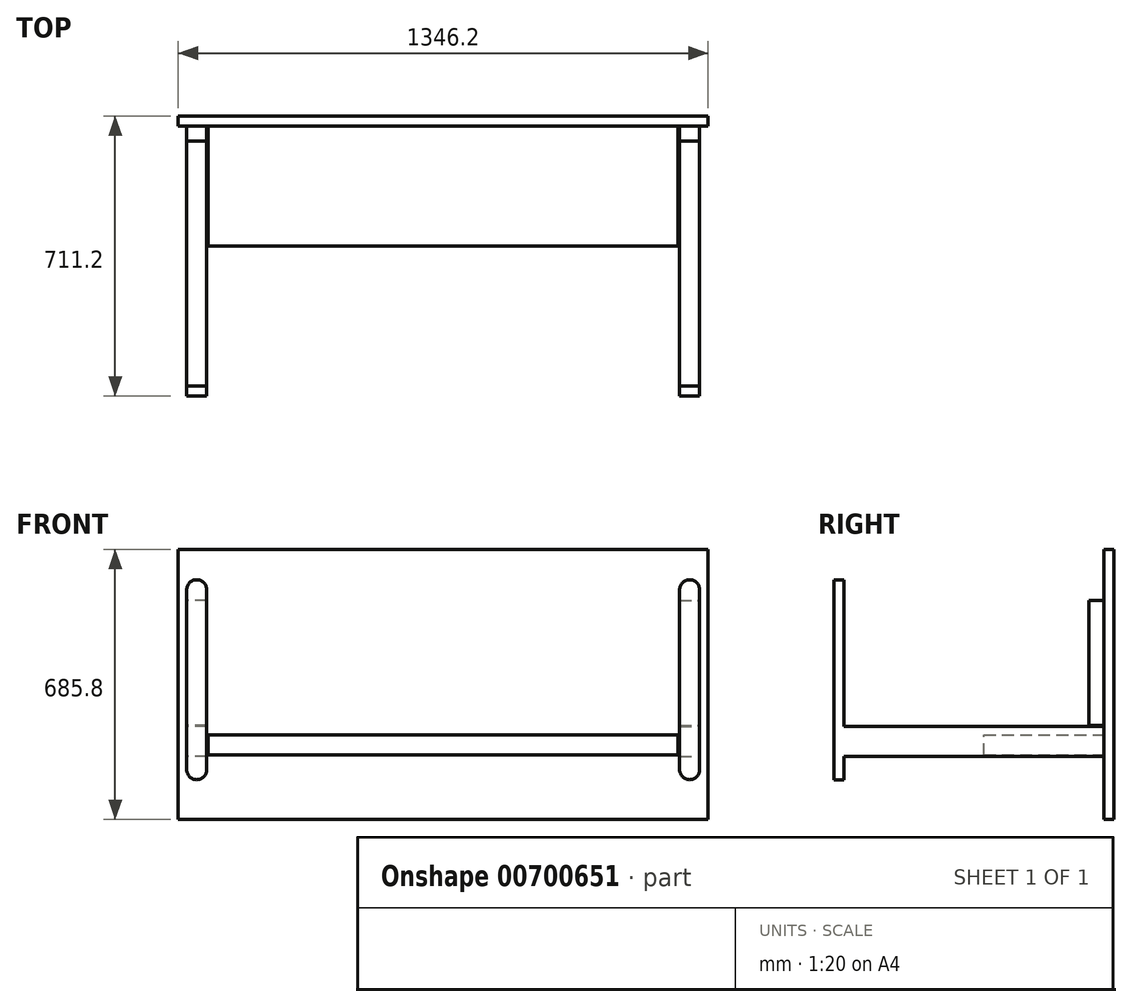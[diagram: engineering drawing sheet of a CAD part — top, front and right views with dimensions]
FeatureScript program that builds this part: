
annotation { "Feature Type Name" : "Feature", "Feature Type Description" : "" }
export const myFeature = defineFeature(function(context is Context, id is Id, definition is map)
    precondition{}
    {
        {
            var Q0;
            Q0=qCreatedBy(makeId("Front.planeOp"),FACE);
            var sketch = newSketch(context, id + "F0", { "sketchPlane" : qUnion([Q0])});
            skLineSegment(sketch, "E0.bottom", {"start": v(393.76, -264.72) * mm, "end": v(-952.44, -264.72) * mm});
            skLineSegment(sketch, "E0.top", {"start": v(393.76, 421.08) * mm, "end": v(-952.44, 421.08) * mm});
            skLineSegment(sketch, "E0.left", {"start": v(393.76, -264.72) * mm, "end": v(393.76, 421.08) * mm});
            skLineSegment(sketch, "E0.right", {"start": v(-952.44, -264.72) * mm, "end": v(-952.44, 421.08) * mm});
            skPoint(sketch, "E0.middle", {"position": v(-279.34, 78.18) * mm});
            skSolve(sketch);
        }
        {
            var Q0;
            Q0 = qSketchRegion(id + "F0", true);
            extrude(context, id + "F1", {"entities" : qUnion([Q0]), "depth" : 25.4 * mm, "offsetDistance" : 25.4 * mm});
        }
        {
            var Q0;
            Q0=makeQuery(id+"F1.opExtrude","CAP_FACE",FACE,{"disambiguationData":[OSD([sQuery(id+"F0.wireOp",EDGE,"E0.bottom"),sQuery(id+"F0.wireOp",EDGE,"E0.top"),sQuery(id+"F0.wireOp",EDGE,"E0.left"),sQuery(id+"F0.wireOp",EDGE,"E0.right")])],"isStart":false});
            var sketch = newSketch(context, id + "F2", { "sketchPlane" : qUnion([Q0])});
            skLineSegment(sketch, "E1", {"start": v(-279.34, 421.08) * mm, "end": v(-279.34, -264.72) * mm});
            skLineSegment(sketch, "E2.bottom", {"start": v(-879.77, -26.15) * mm, "end": v(-930.57, -26.15) * mm});
            skLineSegment(sketch, "E2.top", {"start": v(-879.77, 291.35) * mm, "end": v(-930.57, 291.35) * mm});
            skLineSegment(sketch, "E2.left", {"start": v(-879.77, -26.15) * mm, "end": v(-879.77, 291.35) * mm});
            skLineSegment(sketch, "E2.right", {"start": v(-930.57, -26.15) * mm, "end": v(-930.57, 291.35) * mm});
            skPoint(sketch, "E2.middle", {"position": v(-905.17, 132.6) * mm});
            skPoint(sketch, "E3.MirrorP", {"position": v(346.5, 132.6) * mm});
            skLineSegment(sketch, "E4.MirrorCS", {"start": v(321.1, -26.15) * mm, "end": v(321.1, 291.35) * mm});
            skLineSegment(sketch, "E5.MirrorCS", {"start": v(321.1, 291.35) * mm, "end": v(371.9, 291.35) * mm});
            skLineSegment(sketch, "E6.MirrorCS", {"start": v(371.9, -26.15) * mm, "end": v(371.9, 291.35) * mm});
            skLineSegment(sketch, "E7.MirrorCS", {"start": v(321.1, -26.15) * mm, "end": v(371.9, -26.15) * mm});
            skSolve(sketch);
        }
        {
            var Q0;
            Q0 = qSketchRegion(id + "F2", true);
            extrude(context, id + "F3", {"entities" : qUnion([Q0]), "operationType" : NewBodyOperationType.ADD, "depth" : 38.1 * mm, "offsetDistance" : 25.4 * mm});
        }
        {
            var Q0;
            Q0=makeQuery(id+"F1.opExtrude","CAP_FACE",FACE,{"disambiguationData":[OSD([sQuery(id+"F0.wireOp",EDGE,"E0.bottom"),sQuery(id+"F0.wireOp",EDGE,"E0.top"),sQuery(id+"F0.wireOp",EDGE,"E0.left"),sQuery(id+"F0.wireOp",EDGE,"E0.right")])],"isStart":false});
            var sketch = newSketch(context, id + "F4", { "sketchPlane" : qUnion([Q0])});
            skLineSegment(sketch, "E8.bottom", {"start": v(-880.2, -104.21) * mm, "end": v(-931, -104.21) * mm});
            skLineSegment(sketch, "E8.top", {"start": v(-880.2, -28.01) * mm, "end": v(-931, -28.01) * mm});
            skLineSegment(sketch, "E8.left", {"start": v(-880.2, -104.21) * mm, "end": v(-880.2, -28.01) * mm});
            skLineSegment(sketch, "E8.right", {"start": v(-931, -104.21) * mm, "end": v(-931, -28.01) * mm});
            skPoint(sketch, "E8.middle", {"position": v(-905.6, -66.11) * mm});
            skLineSegment(sketch, "E9", {"start": v(-279.34, 421.08) * mm, "end": v(-279.34, -264.72) * mm});
            skLineSegment(sketch, "E10.MirrorCS", {"start": v(372.32, -104.21) * mm, "end": v(372.32, -28.01) * mm});
            skLineSegment(sketch, "E11.MirrorCS", {"start": v(321.52, -104.21) * mm, "end": v(321.52, -28.01) * mm});
            skLineSegment(sketch, "E12.MirrorCS", {"start": v(321.52, -104.21) * mm, "end": v(372.32, -104.21) * mm});
            skLineSegment(sketch, "E13.MirrorCS", {"start": v(321.52, -28.01) * mm, "end": v(372.32, -28.01) * mm});
            skPoint(sketch, "E14.MirrorP", {"position": v(346.92, -66.11) * mm});
            skSolve(sketch);
        }
        {
            var Q0;
            Q0 = qSketchRegion(id + "F4", true);
            extrude(context, id + "F5", {"entities" : qUnion([Q0]), "operationType" : NewBodyOperationType.ADD, "depth" : 660.4 * mm, "offsetDistance" : 25.4 * mm});
        }
        {
            var Q0;
            Q0=makeQuery(id+"F5.opExtrude","CAP_FACE",FACE,{"disambiguationData":[OSD([sQuery(id+"F4.wireOp",EDGE,"E8.bottom"),sQuery(id+"F4.wireOp",EDGE,"E8.top"),sQuery(id+"F4.wireOp",EDGE,"E8.left"),sQuery(id+"F4.wireOp",EDGE,"E8.right")])],"isStart":false});
            var sketch = newSketch(context, id + "F6", { "sketchPlane" : qUnion([Q0])});
            skLineSegment(sketch, "E15.bottom", {"start": v(-905.6, 344.26) * mm, "end": v(-905.6, 344.26) * mm});
            skLineSegment(sketch, "E15.top", {"start": v(-905.6, -163.74) * mm, "end": v(-905.6, -163.74) * mm});
            skLineSegment(sketch, "E15.left", {"start": v(-880.2, 318.86) * mm, "end": v(-880.2, -138.34) * mm});
            skLineSegment(sketch, "E15.right", {"start": v(-931, 318.86) * mm, "end": v(-931, -138.34) * mm});
            skPoint(sketch, "E15.middle", {"position": v(-905.6, 90.26) * mm});
            skPoint(sketch, "E16.visualSharp", {"position": v(-880.2, 344.26) * mm});
            skArc(sketch, "E16.filletArc", {"start": v(-880.2, 318.86) * mm, "mid": v(-887.64, 336.82) * mm, "end": v(-905.6, 344.26) * mm});
            skPoint(sketch, "E17.visualSharp", {"position": v(-931, 344.26) * mm});
            skArc(sketch, "E17.filletArc", {"start": v(-905.6, 344.26) * mm, "mid": v(-923.56, 336.82) * mm, "end": v(-931, 318.86) * mm});
            skPoint(sketch, "E18.visualSharp", {"position": v(-880.2, -163.74) * mm});
            skArc(sketch, "E18.filletArc", {"start": v(-905.6, -163.74) * mm, "mid": v(-887.64, -156.3) * mm, "end": v(-880.2, -138.34) * mm});
            skPoint(sketch, "E19.visualSharp", {"position": v(-931, -163.74) * mm});
            skArc(sketch, "E19.filletArc", {"start": v(-931, -138.34) * mm, "mid": v(-923.56, -156.3) * mm, "end": v(-905.6, -163.74) * mm});
            skPoint(sketch, "E20.MirrorP", {"position": v(346.92, 90.26) * mm});
            skLineSegment(sketch, "E21.MirrorCS", {"start": v(321.52, 318.86) * mm, "end": v(321.52, -138.34) * mm});
            skLineSegment(sketch, "E22.MirrorCS", {"start": v(372.32, 318.86) * mm, "end": v(372.32, -138.34) * mm});
            skPoint(sketch, "E23.MirrorP", {"position": v(321.52, -163.74) * mm});
            skArc(sketch, "E24.MirrorCS", {"start": v(346.92, -163.74) * mm, "mid": v(328.96, -156.3) * mm, "end": v(321.52, -138.34) * mm});
            skPoint(sketch, "E25.MirrorP", {"position": v(372.32, -163.74) * mm});
            skArc(sketch, "E26.MirrorCS", {"start": v(372.32, -138.34) * mm, "mid": v(364.88, -156.3) * mm, "end": v(346.92, -163.74) * mm});
            skPoint(sketch, "E27.MirrorP", {"position": v(321.52, 344.26) * mm});
            skArc(sketch, "E28.MirrorCS", {"start": v(346.92, 344.26) * mm, "mid": v(364.88, 336.82) * mm, "end": v(372.32, 318.86) * mm});
            skPoint(sketch, "E29.MirrorP", {"position": v(372.32, 344.26) * mm});
            skArc(sketch, "E30.MirrorCS", {"start": v(321.52, 318.86) * mm, "mid": v(328.96, 336.82) * mm, "end": v(346.92, 344.26) * mm});
            skSolve(sketch);
        }
        {
            var Q0;
            Q0 = qSketchRegion(id + "F6", true);
            extrude(context, id + "F7", {"entities" : qUnion([Q0]), "operationType" : NewBodyOperationType.ADD, "depth" : 25.4 * mm, "offsetDistance" : 25.4 * mm});
        }
        {
            var Q0;
            {var subQ2=sQuery(id+"F2.wireOp",EDGE,"E1");Q0=makeQuery(id+"F2.imprint","IMPRINT",FACE,{"disambiguationData":[TD([[makeQuery(id+"F2.imprint","IMPRINT",EDGE,{"derivedFrom":subQ2}),-1.0]])]});}
            var sketch = newSketch(context, id + "F8", { "sketchPlane" : qUnion([Q0])});
            skLineSegment(sketch, "E31.bottom", {"start": v(-876.53, -101.2) * mm, "end": v(317.27, -101.2) * mm});
            skLineSegment(sketch, "E31.top", {"start": v(-876.53, -50.4) * mm, "end": v(317.27, -50.4) * mm});
            skLineSegment(sketch, "E31.left", {"start": v(-876.53, -101.2) * mm, "end": v(-876.53, -50.4) * mm});
            skLineSegment(sketch, "E31.right", {"start": v(317.27, -101.2) * mm, "end": v(317.27, -50.4) * mm});
            skPoint(sketch, "E31.middle", {"position": v(-279.63, -75.8) * mm});
            skSolve(sketch);
        }
        {
            var Q0;
            Q0 = qSketchRegion(id + "F8", true);
            extrude(context, id + "F9", {"entities" : qUnion([Q0]), "operationType" : NewBodyOperationType.ADD, "depth" : 304.8 * mm, "offsetDistance" : 25.4 * mm});
        }
    });
